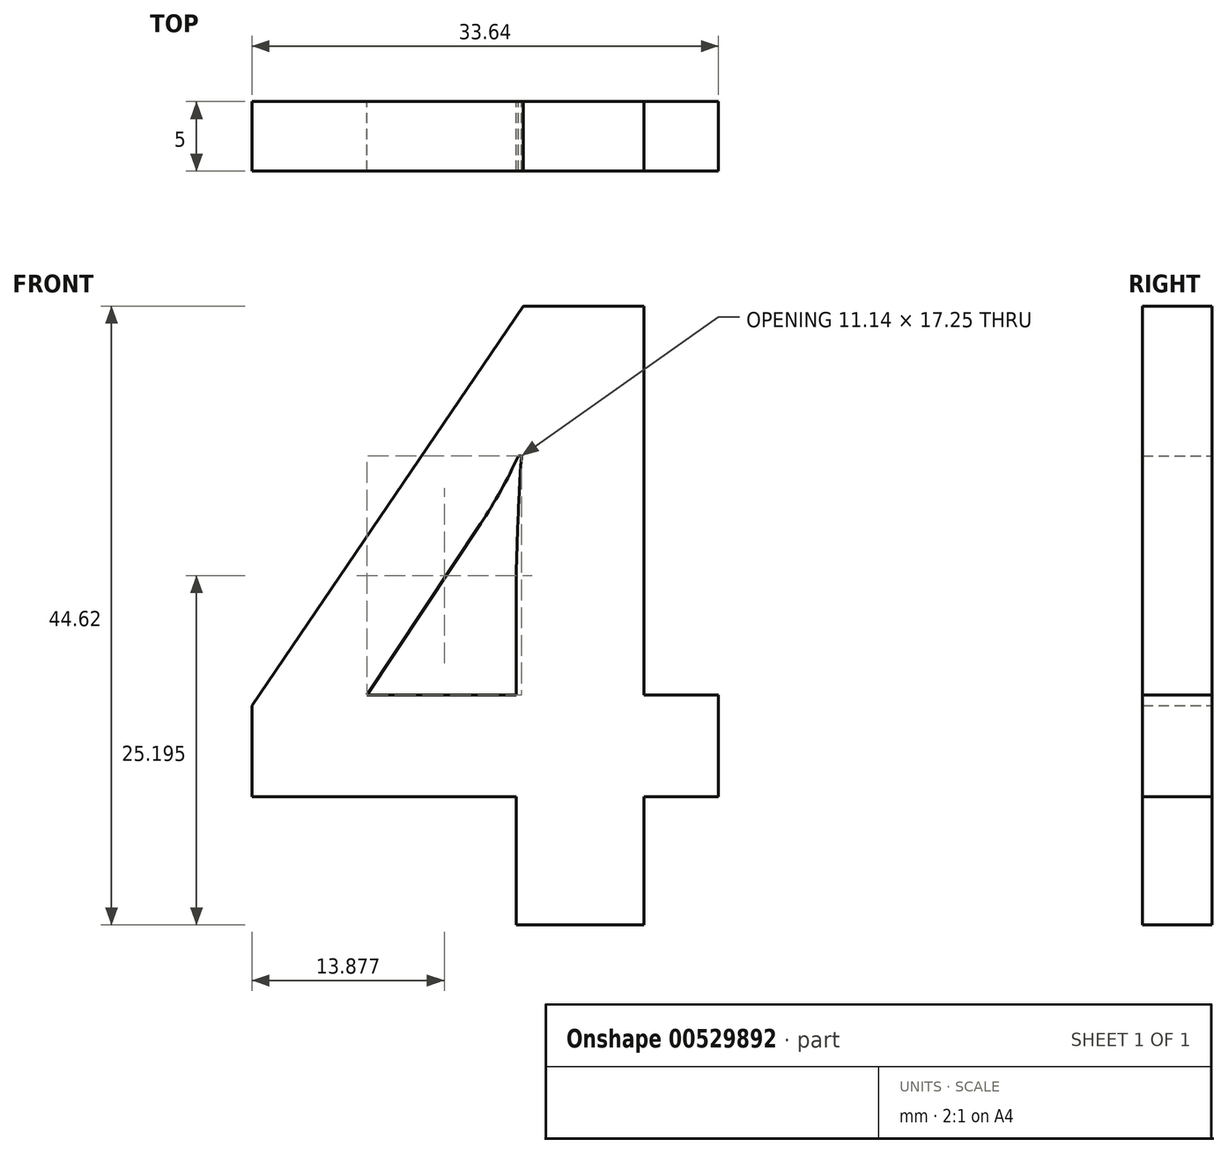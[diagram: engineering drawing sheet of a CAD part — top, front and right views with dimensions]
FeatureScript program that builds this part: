
annotation { "Feature Type Name" : "Feature", "Feature Type Description" : "" }
export const myFeature = defineFeature(function(context is Context, id is Id, definition is map)
    precondition{}
    {
        {
            var Q0;
            Q0=qCreatedBy(makeId("Front.planeOp"),FACE);
            var sketch = newSketch(context, id + "F0", { "sketchPlane" : qUnion([Q0])});
            skText(sketch, "E0", { "text": "4", "fontName": "OpenSans-Bold.ttf"});
            const initialGuessF0  = {"E0": [-0.0587, 0.01454, 1, 0, 0.045]};
            skSetInitialGuess(sketch, initialGuessF0);
            skSolve(sketch);
        }
        {
            var Q0;
            Q0=makeQuery(id+"F0.imprint","IMPRINT",FACE,{"disambiguationData":[TD([[makeQuery(id+"F0.imprint","IMPRINT",EDGE,{"derivedFrom":sQuery(id+"F0.wireOp",EDGE,"E0.sketch_text.stroke-0")}),-1.0]])]});
            extrude(context, id + "F1", {"entities" : qUnion([Q0]), "depth" : 5 * mm, "offsetDistance" : 25 * mm});
        }
    });
